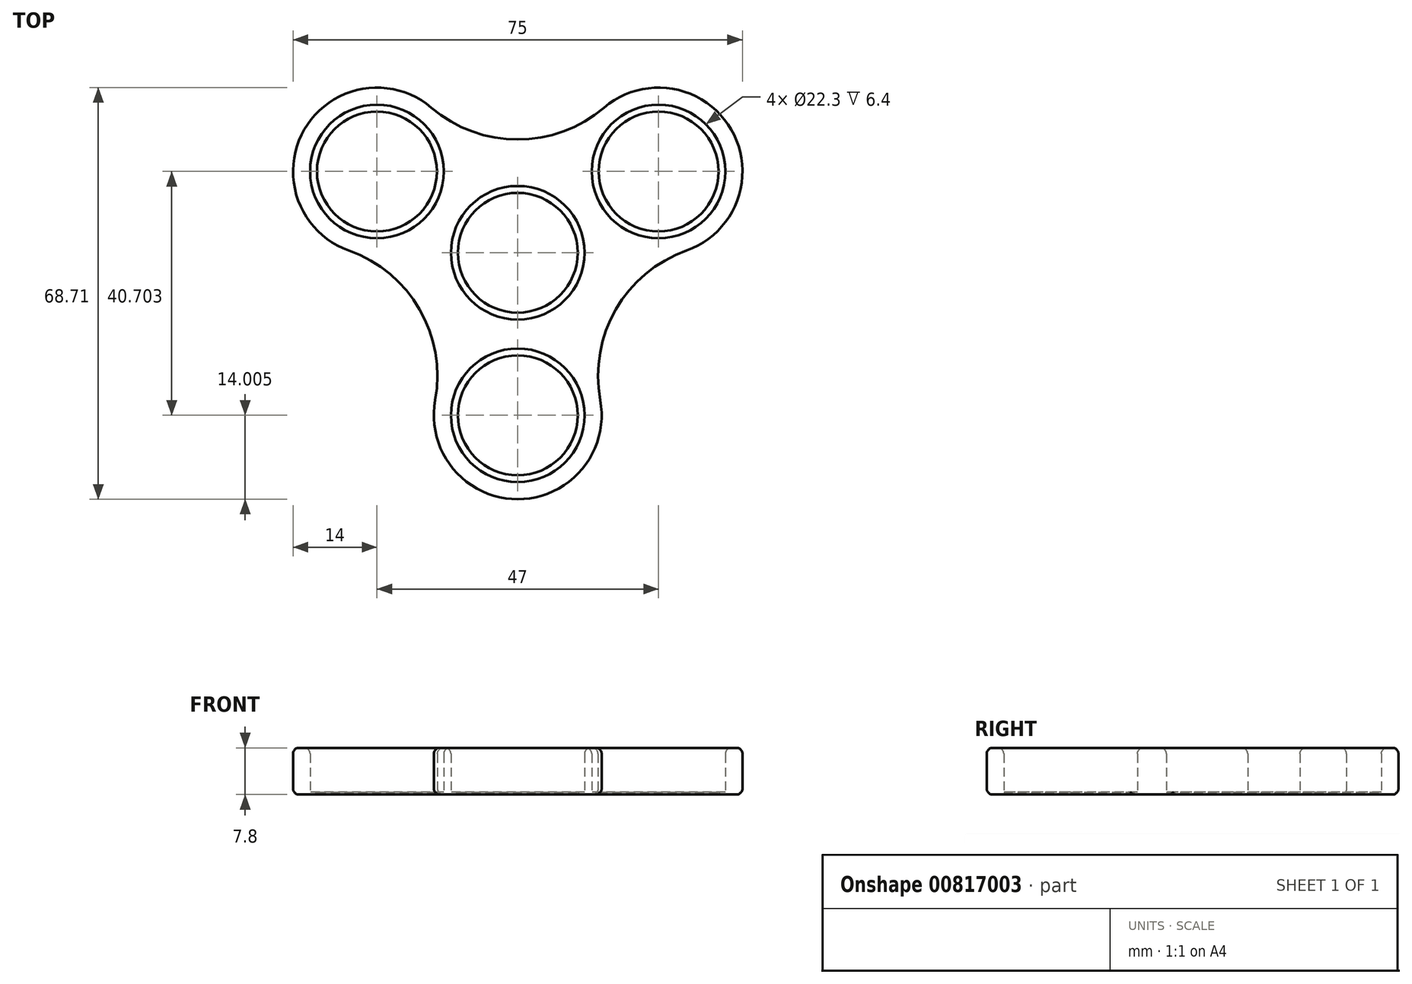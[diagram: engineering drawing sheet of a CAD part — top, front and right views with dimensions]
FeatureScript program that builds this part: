
annotation { "Feature Type Name" : "Feature", "Feature Type Description" : "" }
export const myFeature = defineFeature(function(context is Context, id is Id, definition is map)
    precondition{}
    {
        {
            var Q0;
            Q0=qCreatedBy(makeId("Top.planeOp"),FACE);
            var sketch = newSketch(context, id + "F0", { "sketchPlane" : qUnion([Q0])});
            skCircle(sketch, "E0.cCircle", {"center": v(0, 0) * mm, "radius": 13.57 * mm, "construction": true});
            skLineSegment(sketch, "E0.0", {"start": v(-23.5, 13.57) * mm, "end": v(23.5, 13.57) * mm, "construction": true});
            skLineSegment(sketch, "E0.1", {"start": v(23.5, 13.57) * mm, "end": v(0, -27.14) * mm, "construction": true});
            skLineSegment(sketch, "E0.2", {"start": v(0, -27.14) * mm, "end": v(-23.5, 13.57) * mm, "construction": true});
            skPoint(sketch, "E0.0.midPoint", {"position": v(0, 13.57) * mm});
            skCircle(sketch, "E1", {"center": v(-23.5, 13.57) * mm, "radius": 11.15 * mm});
            skCircle(sketch, "E2", {"center": v(-23.5, 13.57) * mm, "radius": 14 * mm});
            skCircle(sketch, "E3", {"center": v(0, -27.14) * mm, "radius": 11.15 * mm});
            skCircle(sketch, "E4", {"center": v(0, -27.14) * mm, "radius": 14 * mm});
            skCircle(sketch, "E5", {"center": v(23.5, 13.57) * mm, "radius": 14 * mm});
            skCircle(sketch, "E6", {"center": v(23.5, 13.57) * mm, "radius": 11.15 * mm});
            skCircle(sketch, "E7", {"center": v(0, 0) * mm, "radius": 41.14 * mm, "construction": true});
            skPoint(sketch, "E8", {"position": v(-11.75, -6.78) * mm});
            skPoint(sketch, "E9", {"position": v(11.75, -6.78) * mm});
            skLineSegment(sketch, "E10", {"start": v(0, 0) * mm, "end": v(-11.75, -6.78) * mm, "construction": true});
            skLineSegment(sketch, "E11", {"start": v(0, 0) * mm, "end": v(0, 13.57) * mm, "construction": true});
            skLineSegment(sketch, "E12", {"start": v(0, 0) * mm, "end": v(11.75, -6.78) * mm, "construction": true});
            skLineSegment(sketch, "E13", {"start": v(-11.75, -6.78) * mm, "end": v(-35.62, -20.57) * mm, "construction": true});
            skLineSegment(sketch, "E14", {"start": v(11.75, -6.78) * mm, "end": v(35.62, -20.57) * mm, "construction": true});
            skLineSegment(sketch, "E15", {"start": v(0, 13.57) * mm, "end": v(0, 41.14) * mm, "construction": true});
            skCircle(sketch, "E16", {"center": v(0, 41.14) * mm, "radius": 22.22 * mm});
            skCircle(sketch, "E17", {"center": v(-35.62, -20.57) * mm, "radius": 22.22 * mm});
            skCircle(sketch, "E18", {"center": v(35.62, -20.57) * mm, "radius": 22.22 * mm});
            skCircle(sketch, "E19", {"center": v(0, 0) * mm, "radius": 11.15 * mm});
            skSolve(sketch);
        }
        {
            var Q0;
            Q0=makeQuery(id+"F0.imprint","IMPRINT",FACE,{"disambiguationData":[TD([[makeQuery(id+"F0.imprint","IMPRINT",EDGE,{"derivedFrom":sQuery(id+"F0.wireOp",EDGE,"E19")}),-1.0]])]});
            var Q1;
            Q1=makeQuery(id+"F0.imprint","IMPRINT",FACE,{"disambiguationData":[TD([[makeQuery(id+"F0.imprint","IMPRINT",EDGE,{"derivedFrom":sQuery(id+"F0.wireOp",EDGE,"E1")}),-1.0]])]});
            var Q2;
            Q2=makeQuery(id+"F0.imprint","IMPRINT",FACE,{"disambiguationData":[TD([[makeQuery(id+"F0.imprint","IMPRINT",EDGE,{"derivedFrom":sQuery(id+"F0.wireOp",EDGE,"E6")}),-1.0]])]});
            var Q3;
            Q3=makeQuery(id+"F0.imprint","IMPRINT",FACE,{"disambiguationData":[TD([[makeQuery(id+"F0.imprint","IMPRINT",EDGE,{"derivedFrom":sQuery(id+"F0.wireOp",EDGE,"E3")}),-1.0]])]});
            extrude(context, id + "F1", {"entities" : qUnion([Q0, Q1, Q2, Q3]), "depth" : 7.8 * mm, "offsetDistance" : 25 * mm});
        }
        {
            var Q0;
            Q0=makeQuery(id+"F1.opExtrude","CAP_FACE",FACE,{"disambiguationData":[OSD([sQuery(id+"F0.wireOp",EDGE,"E1"),sQuery(id+"F0.wireOp",EDGE,"E2"),sQuery(id+"F0.wireOp",EDGE,"E3"),sQuery(id+"F0.wireOp",EDGE,"E4"),sQuery(id+"F0.wireOp",EDGE,"E5"),sQuery(id+"F0.wireOp",EDGE,"E6"),sQuery(id+"F0.wireOp",EDGE,"E16"),sQuery(id+"F0.wireOp",EDGE,"E17"),sQuery(id+"F0.wireOp",EDGE,"E18"),sQuery(id+"F0.wireOp",EDGE,"E19")])],"isStart":true});
            var sketch = newSketch(context, id + "F2", { "sketchPlane" : qUnion([Q0])});
            skCircle(sketch, "E20", {"center": v(0, 27.14) * mm, "radius": 10 * mm});
            skCircle(sketch, "E21", {"center": v(23.5, -13.57) * mm, "radius": 10 * mm});
            skCircle(sketch, "E22", {"center": v(-23.5, -13.57) * mm, "radius": 10 * mm});
            skCircle(sketch, "E23", {"center": v(0, 27.14) * mm, "radius": 11.15 * mm});
            skCircle(sketch, "E24", {"center": v(23.5, -13.57) * mm, "radius": 11.15 * mm});
            skCircle(sketch, "E25", {"center": v(-23.5, -13.57) * mm, "radius": 11.15 * mm});
            skSolve(sketch);
        }
        {
            var Q0;
            Q0=qSketchRegion(id+"F2",true);
            extrude(context, id + "F3", {"entities" : qUnion([Q0]), "operationType" : NewBodyOperationType.ADD, "oppositeDirection" : true, "depth" : 0.4 * mm, "offsetDistance" : 25 * mm});
        }
        {
            var Q0;
            Q0=makeQuery(id+"F3.boolean.opBoolean","MERGE",FACE,{"derivedFrom":[makeQuery(id+"F1.opExtrude","CAP_FACE",FACE,{"disambiguationData":[OSD([sQuery(id+"F0.wireOp",EDGE,"E1"),sQuery(id+"F0.wireOp",EDGE,"E2"),sQuery(id+"F0.wireOp",EDGE,"E3"),sQuery(id+"F0.wireOp",EDGE,"E4"),sQuery(id+"F0.wireOp",EDGE,"E5"),sQuery(id+"F0.wireOp",EDGE,"E6"),sQuery(id+"F0.wireOp",EDGE,"E16"),sQuery(id+"F0.wireOp",EDGE,"E17"),sQuery(id+"F0.wireOp",EDGE,"E18"),sQuery(id+"F0.wireOp",EDGE,"E19")])],"isStart":true}),makeQuery(id+"F3.opExtrude","CAP_FACE",FACE,{"disambiguationData":[OSD([sQuery(id+"F2.wireOp",EDGE,"E20"),sQuery(id+"F2.wireOp",EDGE,"E23")])],"isStart":true}),makeQuery(id+"F3.opExtrude","CAP_FACE",FACE,{"disambiguationData":[OSD([sQuery(id+"F2.wireOp",EDGE,"E21"),sQuery(id+"F2.wireOp",EDGE,"E24")])],"isStart":true}),makeQuery(id+"F3.opExtrude","CAP_FACE",FACE,{"disambiguationData":[OSD([sQuery(id+"F2.wireOp",EDGE,"E22"),sQuery(id+"F2.wireOp",EDGE,"E25")])],"isStart":true})]});
            var sketch = newSketch(context, id + "F4", { "sketchPlane" : qUnion([Q0])});
            skCircle(sketch, "E26", {"center": v(0, 0) * mm, "radius": 10 * mm});
            skCircle(sketch, "E27", {"center": v(0, 0) * mm, "radius": 11.15 * mm});
            skSolve(sketch);
        }
        {
            var Q0;
            Q0=qSketchRegion(id+"F4",true);
            extrude(context, id + "F5", {"entities" : qUnion([Q0]), "operationType" : NewBodyOperationType.ADD, "oppositeDirection" : true, "depth" : 0.4 * mm, "offsetDistance" : 25 * mm});
        }
        {
            var Q0;
            Q0=makeQuery(id+"F1.opExtrude","CAP_EDGE",EDGE,{"disambiguationData":[OSD([sQuery(id+"F0.wireOp",EDGE,"E1")])],"isStart":false});
            var Q1;
            Q1=makeQuery(id+"F1.opExtrude","CAP_EDGE",EDGE,{"disambiguationData":[OSD([sQuery(id+"F0.wireOp",EDGE,"E3")])],"isStart":false});
            var Q2;
            Q2=makeQuery(id+"F1.opExtrude","CAP_EDGE",EDGE,{"disambiguationData":[OSD([sQuery(id+"F0.wireOp",EDGE,"E19")])],"isStart":false});
            var Q3;
            Q3=makeQuery(id+"F1.opExtrude","CAP_EDGE",EDGE,{"disambiguationData":[OSD([sQuery(id+"F0.wireOp",EDGE,"E6")])],"isStart":false});
            var Q4;
            Q4=makeQuery(id+"F1.opExtrude","CAP_FACE",FACE,{"disambiguationData":[OSD([sQuery(id+"F0.wireOp",EDGE,"E1"),sQuery(id+"F0.wireOp",EDGE,"E2"),sQuery(id+"F0.wireOp",EDGE,"E3"),sQuery(id+"F0.wireOp",EDGE,"E4"),sQuery(id+"F0.wireOp",EDGE,"E5"),sQuery(id+"F0.wireOp",EDGE,"E6"),sQuery(id+"F0.wireOp",EDGE,"E16"),sQuery(id+"F0.wireOp",EDGE,"E17"),sQuery(id+"F0.wireOp",EDGE,"E18"),sQuery(id+"F0.wireOp",EDGE,"E19")])],"isStart":false});
            var Q5;
            Q5=makeQuery(id+"F5.boolean.opBoolean","MERGE",FACE,{"derivedFrom":[makeQuery(id+"F3.boolean.opBoolean","MERGE",FACE,{"derivedFrom":[makeQuery(id+"F1.opExtrude","CAP_FACE",FACE,{"disambiguationData":[OSD([sQuery(id+"F0.wireOp",EDGE,"E1"),sQuery(id+"F0.wireOp",EDGE,"E2"),sQuery(id+"F0.wireOp",EDGE,"E3"),sQuery(id+"F0.wireOp",EDGE,"E4"),sQuery(id+"F0.wireOp",EDGE,"E5"),sQuery(id+"F0.wireOp",EDGE,"E6"),sQuery(id+"F0.wireOp",EDGE,"E16"),sQuery(id+"F0.wireOp",EDGE,"E17"),sQuery(id+"F0.wireOp",EDGE,"E18"),sQuery(id+"F0.wireOp",EDGE,"E19")])],"isStart":true}),makeQuery(id+"F3.opExtrude","CAP_FACE",FACE,{"disambiguationData":[OSD([sQuery(id+"F2.wireOp",EDGE,"E20"),sQuery(id+"F2.wireOp",EDGE,"E23")])],"isStart":true}),makeQuery(id+"F3.opExtrude","CAP_FACE",FACE,{"disambiguationData":[OSD([sQuery(id+"F2.wireOp",EDGE,"E21"),sQuery(id+"F2.wireOp",EDGE,"E24")])],"isStart":true}),makeQuery(id+"F3.opExtrude","CAP_FACE",FACE,{"disambiguationData":[OSD([sQuery(id+"F2.wireOp",EDGE,"E22"),sQuery(id+"F2.wireOp",EDGE,"E25")])],"isStart":true})]}),makeQuery(id+"F5.opExtrude","CAP_FACE",FACE,{"disambiguationData":[OSD([sQuery(id+"F4.wireOp",EDGE,"E26"),sQuery(id+"F4.wireOp",EDGE,"E27")])],"isStart":true})]});
            fillet(context, id + "F6", {"entities" : qUnion([Q0, Q1, Q2, Q3, Q4, Q5]), "radius" : 1 * mm, "tangentPropagation" : true, "allowEdgeOverflow" : false});
        }
    });
